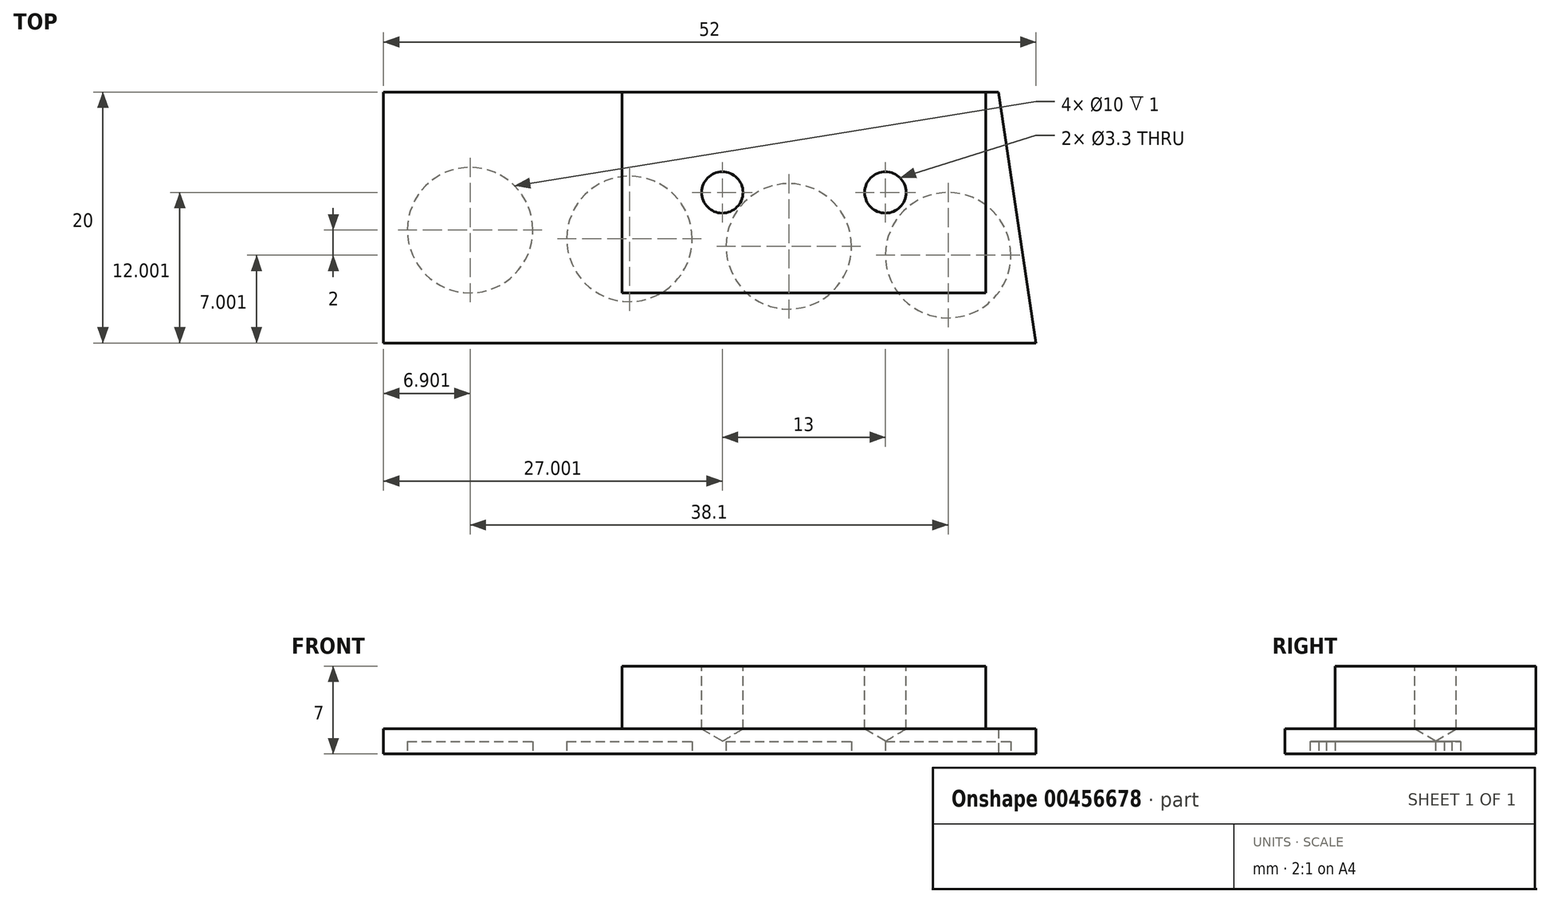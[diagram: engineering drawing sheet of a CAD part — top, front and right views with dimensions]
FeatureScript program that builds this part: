
annotation { "Feature Type Name" : "Feature", "Feature Type Description" : "" }
export const myFeature = defineFeature(function(context is Context, id is Id, definition is map)
    precondition{}
    {
        {
            var Q0;
            Q0=qCreatedBy(makeId("Top.planeOp"),FACE);
            var sketch = newSketch(context, id + "F0", { "sketchPlane" : qUnion([Q0])});
            skLineSegment(sketch, "E0", {"start": v(-25.77, 9.48) * mm, "end": v(-25.77, -10.52) * mm});
            skLineSegment(sketch, "E1", {"start": v(-25.77, -10.52) * mm, "end": v(26.23, -10.52) * mm});
            skLineSegment(sketch, "E2", {"start": v(-25.77, 9.48) * mm, "end": v(23.23, 9.48) * mm});
            skLineSegment(sketch, "E3", {"start": v(19.23, 15.1) * mm, "end": v(19.23, -21.8) * mm, "construction": true});
            skLineSegment(sketch, "E4", {"start": v(6.53, 15.1) * mm, "end": v(6.53, -21.56) * mm, "construction": true});
            skLineSegment(sketch, "E5", {"start": v(-6.17, 14.64) * mm, "end": v(-6.17, -20.64) * mm, "construction": true});
            skLineSegment(sketch, "E6", {"start": v(-18.87, 14.87) * mm, "end": v(-18.87, -20.18) * mm, "construction": true});
            skLineSegment(sketch, "E7", {"start": v(23.23, 9.48) * mm, "end": v(26.23, -10.52) * mm});
            skSolve(sketch);
        }
        {
            var Q0;
            Q0=makeQuery(id+"F0.imprint","IMPRINT",FACE,{"disambiguationData":[TD([[makeQuery(id+"F0.imprint","IMPRINT",EDGE,{"derivedFrom":sQuery(id+"F0.wireOp",EDGE,"E0")}),1.0]])]});
            extrude(context, id + "F1", {"entities" : qUnion([Q0]), "depth" : 2 * mm, "offsetDistance" : 25 * mm});
        }
        {
            var Q0;
            Q0=makeQuery(id+"F1.opExtrude","CAP_FACE",FACE,{"disambiguationData":[OSD([sQuery(id+"F0.wireOp",EDGE,"E0"),sQuery(id+"F0.wireOp",EDGE,"E1"),sQuery(id+"F0.wireOp",EDGE,"E2"),sQuery(id+"F0.wireOp",EDGE,"E7")])],"isStart":true});
            var sketch = newSketch(context, id + "F2", { "sketchPlane" : qUnion([Q0])});
            skLineSegment(sketch, "E8", {"start": v(19.23, -13.94) * mm, "end": v(19.23, 20.98) * mm, "construction": true});
            skLineSegment(sketch, "E9", {"start": v(6.53, -13.73) * mm, "end": v(6.53, 19.36) * mm, "construction": true});
            skLineSegment(sketch, "E10", {"start": v(-6.17, -13.52) * mm, "end": v(-6.17, 15.9) * mm, "construction": true});
            skLineSegment(sketch, "E11", {"start": v(-18.87, -13.73) * mm, "end": v(-18.87, 16.76) * mm, "construction": true});
            skCircle(sketch, "E12", {"center": v(19.23, 3.52) * mm, "radius": 5 * mm});
            skCircle(sketch, "E13", {"center": v(-18.87, 1.52) * mm, "radius": 5 * mm});
            skCircle(sketch, "E14", {"center": v(-6.17, 2.22) * mm, "radius": 5 * mm});
            skCircle(sketch, "E15", {"center": v(6.53, 2.82) * mm, "radius": 5 * mm});
            skSolve(sketch);
        }
        {
            var Q0;
            Q0=makeQuery(id+"F2.imprint","IMPRINT",FACE,{"disambiguationData":[TD([[makeQuery(id+"F2.imprint","IMPRINT",EDGE,{"derivedFrom":sQuery(id+"F2.wireOp",EDGE,"E12")}),1.0]])]});
            var Q1;
            Q1=makeQuery(id+"F2.imprint","IMPRINT",FACE,{"disambiguationData":[TD([[makeQuery(id+"F2.imprint","IMPRINT",EDGE,{"derivedFrom":sQuery(id+"F2.wireOp",EDGE,"E15")}),1.0]])]});
            var Q2;
            Q2=makeQuery(id+"F2.imprint","IMPRINT",FACE,{"disambiguationData":[TD([[makeQuery(id+"F2.imprint","IMPRINT",EDGE,{"derivedFrom":sQuery(id+"F2.wireOp",EDGE,"E14")}),1.0]])]});
            var Q3;
            Q3=makeQuery(id+"F2.imprint","IMPRINT",FACE,{"disambiguationData":[TD([[makeQuery(id+"F2.imprint","IMPRINT",EDGE,{"derivedFrom":sQuery(id+"F2.wireOp",EDGE,"E13")}),1.0]])]});
            extrude(context, id + "F3", {"entities" : qUnion([Q0, Q1, Q2, Q3]), "operationType" : NewBodyOperationType.REMOVE, "oppositeDirection" : true, "depth" : 1 * mm});
        }
        {
            var Q0;
            Q0=makeQuery(id+"F1.opExtrude","CAP_FACE",FACE,{"disambiguationData":[OSD([sQuery(id+"F0.wireOp",EDGE,"E0"),sQuery(id+"F0.wireOp",EDGE,"E1"),sQuery(id+"F0.wireOp",EDGE,"E2"),sQuery(id+"F0.wireOp",EDGE,"E7")])],"isStart":false});
            var sketch = newSketch(context, id + "F4", { "sketchPlane" : qUnion([Q0])});
            skLineSegment(sketch, "E16.bottom", {"start": v(-6.77, 9.48) * mm, "end": v(22.23, 9.48) * mm});
            skLineSegment(sketch, "E16.top", {"start": v(-6.77, -6.52) * mm, "end": v(22.23, -6.52) * mm});
            skLineSegment(sketch, "E16.left", {"start": v(-6.77, 9.48) * mm, "end": v(-6.77, -6.52) * mm});
            skLineSegment(sketch, "E16.right", {"start": v(22.23, 9.48) * mm, "end": v(22.23, -6.52) * mm});
            skSolve(sketch);
        }
        {
            var Q0;
            Q0=makeQuery(id+"F4.imprint","IMPRINT",FACE,{"disambiguationData":[TD([[makeQuery(id+"F4.imprint","IMPRINT",EDGE,{"derivedFrom":sQuery(id+"F4.wireOp",EDGE,"E16.bottom")}),-1.0]])]});
            extrude(context, id + "F5", {"entities" : qUnion([Q0]), "operationType" : NewBodyOperationType.ADD, "depth" : 5 * mm, "offsetDistance" : 25 * mm});
        }
        {
            var Q0;
            Q0=makeQuery(id+"F5.opExtrude","CAP_FACE",FACE,{"disambiguationData":[OSD([sQuery(id+"F4.wireOp",EDGE,"E16.bottom"),sQuery(id+"F4.wireOp",EDGE,"E16.top"),sQuery(id+"F4.wireOp",EDGE,"E16.left"),sQuery(id+"F4.wireOp",EDGE,"E16.right")])],"isStart":false});
            var sketch = newSketch(context, id + "F6", { "sketchPlane" : qUnion([Q0])});
            skLineSegment(sketch, "E17", {"start": v(-35.76, 1.48) * mm, "end": v(39.69, 1.48) * mm, "construction": true});
            skLineSegment(sketch, "E18", {"start": v(1.23, 18.73) * mm, "end": v(1.23, -20.13) * mm, "construction": true});
            skLineSegment(sketch, "E19", {"start": v(14.23, 18.36) * mm, "end": v(14.23, -21.21) * mm, "construction": true});
            skCircle(sketch, "E20", {"center": v(1.23, 1.48) * mm, "radius": 2 * mm});
            skCircle(sketch, "E21", {"center": v(14.23, 1.48) * mm, "radius": 2 * mm});
            skSolve(sketch);
        }
        {
            var Q0;
            Q0=sQuery(id+"F6.wireOp",VERTEX,"E20.center");
            var Q1;
            Q1=sQuery(id+"F6.wireOp",VERTEX,"E21.center");
            var Q2;
            Q2=makeQuery(id+"F1.opExtrude","SWEPT_BODY",BODY,{"disambiguationData":[OSD([sQuery(id+"F0.wireOp",EDGE,"E0"),sQuery(id+"F0.wireOp",EDGE,"E1"),sQuery(id+"F0.wireOp",EDGE,"E2"),sQuery(id+"F0.wireOp",EDGE,"E7")])]});
            hole(context, id + "F7", {"style" : HoleStyle.SIMPLE, "endStyle" : HoleEndStyle.BLIND, "standardTappedOrClearance" : lookupTablePath({ "standard" : "ISO", "engagement" : "75%", "pitch" : "0.7 mm", "size" : "M4", "type" : "Tapped" }), "standardBlindInLast" : lookupTablePath({ "standard" : "ISO", "engagement" : "75%", "pitch" : "0.7 mm", "size" : "M4", "type" : "Tapped" }), "holeDiameter" : 3.3 * mm, "showTappedDepth" : true, "holeDepth" : 5 * mm, "tappedDepth" : 2.9 * mm, "tapClearance" : 3, "startFromSketch" : true, "locations" : qUnion([Q0, Q1]), "scope" : qUnion([Q2]), "majorDiameter" : 4 * mm});
        }
    });
